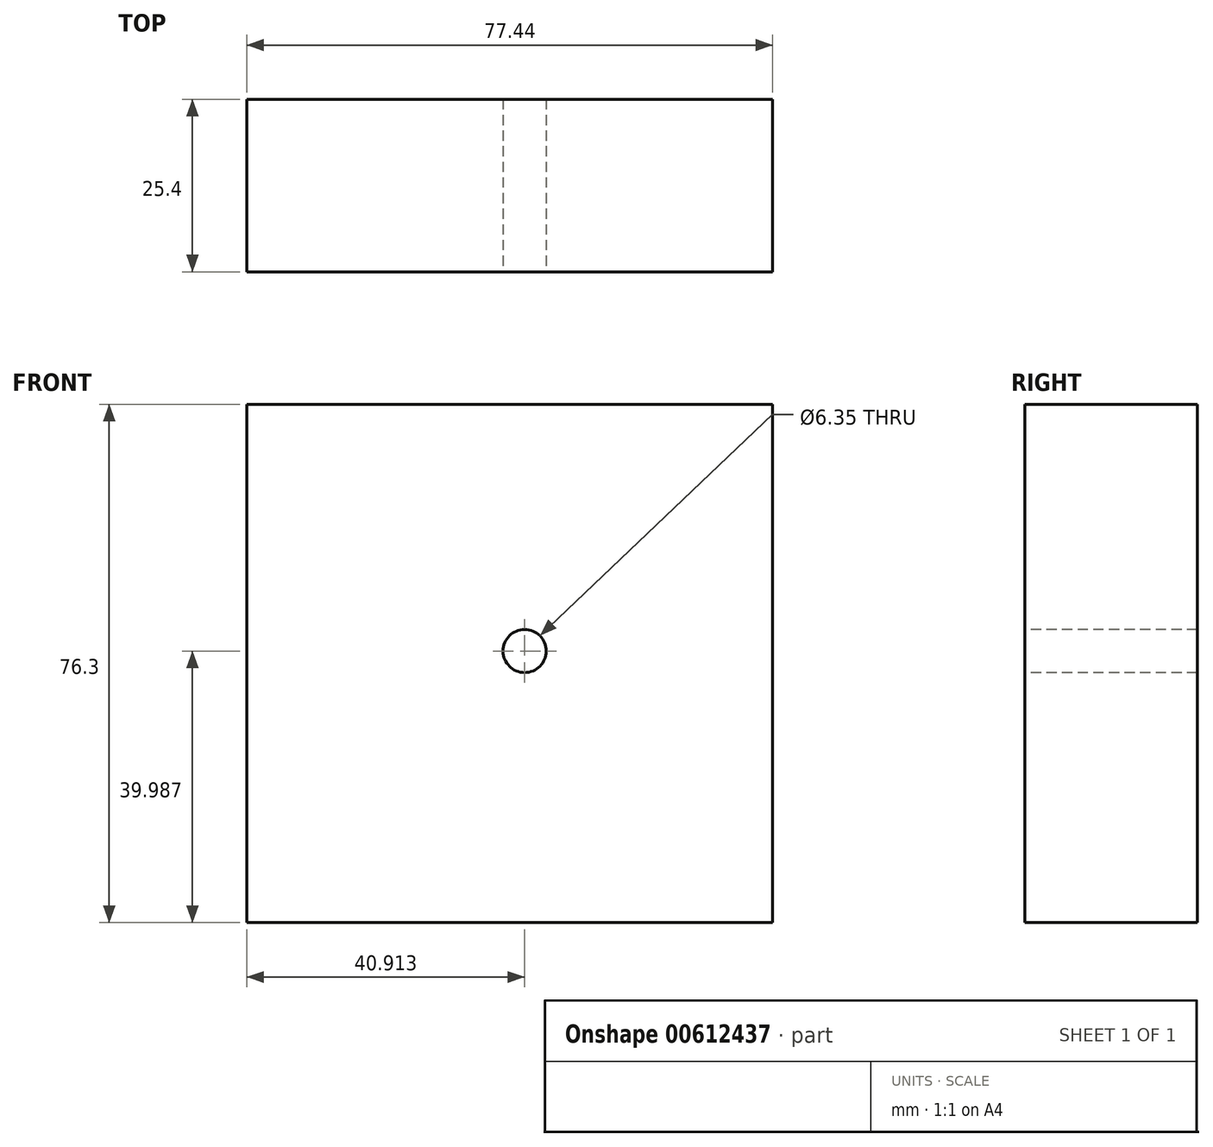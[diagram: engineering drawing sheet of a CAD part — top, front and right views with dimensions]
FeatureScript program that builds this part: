
annotation { "Feature Type Name" : "Feature", "Feature Type Description" : "" }
export const myFeature = defineFeature(function(context is Context, id is Id, definition is map)
    precondition{}
    {
        {
            var Q0;
            Q0=qCreatedBy(makeId("Front.planeOp"),FACE);
            var sketch = newSketch(context, id + "F0", { "sketchPlane" : qUnion([Q0])});
            skLineSegment(sketch, "E0.bottom", {"start": v(0, 0) * mm, "end": v(-77.44, 0) * mm});
            skLineSegment(sketch, "E0.top", {"start": v(0, 76.3) * mm, "end": v(-77.44, 76.3) * mm});
            skLineSegment(sketch, "E0.left", {"start": v(0, 0) * mm, "end": v(0, 76.3) * mm});
            skLineSegment(sketch, "E0.right", {"start": v(-77.44, 0) * mm, "end": v(-77.44, 76.3) * mm});
            skSolve(sketch);
        }
        {
            var Q0;
            Q0=makeQuery(id+"F0.imprint","IMPRINT",FACE,{"disambiguationData":[TD([[makeQuery(id+"F0.imprint","IMPRINT",EDGE,{"derivedFrom":sQuery(id+"F0.wireOp",EDGE,"E0.bottom")}),-1.0]])]});
            extrude(context, id + "F1", {"entities" : qUnion([Q0]), "depth" : 25.4 * mm, "offsetDistance" : 25.4 * mm});
        }
        {
            var Q0;
            Q0=makeQuery(id+"F1.opExtrude","CAP_FACE",FACE,{"disambiguationData":[OSD([sQuery(id+"F0.wireOp",EDGE,"E0.bottom"),sQuery(id+"F0.wireOp",EDGE,"E0.top"),sQuery(id+"F0.wireOp",EDGE,"E0.left"),sQuery(id+"F0.wireOp",EDGE,"E0.right")])],"isStart":false});
            var sketch = newSketch(context, id + "F2", { "sketchPlane" : qUnion([Q0])});
            skCircle(sketch, "E1", {"center": v(-36.53, 39.99) * mm, "radius": 27.75 * mm});
            skSolve(sketch);
        }
        {
            var Q0;
            Q0=sQuery(id+"F2.wireOp",VERTEX,"E1.center");
            var Q1;
            Q1=makeQuery(id+"F1.opExtrude","SWEPT_BODY",BODY,{"disambiguationData":[OSD([sQuery(id+"F0.wireOp",EDGE,"E0.bottom"),sQuery(id+"F0.wireOp",EDGE,"E0.top"),sQuery(id+"F0.wireOp",EDGE,"E0.left"),sQuery(id+"F0.wireOp",EDGE,"E0.right")])]});
            hole(context, id + "F3", {"style" : HoleStyle.SIMPLE, "endStyle" : HoleEndStyle.THROUGH, "holeDiameter" : 6.35 * mm, "majorDiameter" : 6.35 * mm, "isTappedThrough" : true, "tappedDepth" : 12.7 * mm, "tapClearance" : 3, "locations" : qUnion([Q0]), "scope" : qUnion([Q1])});
        }
    });
